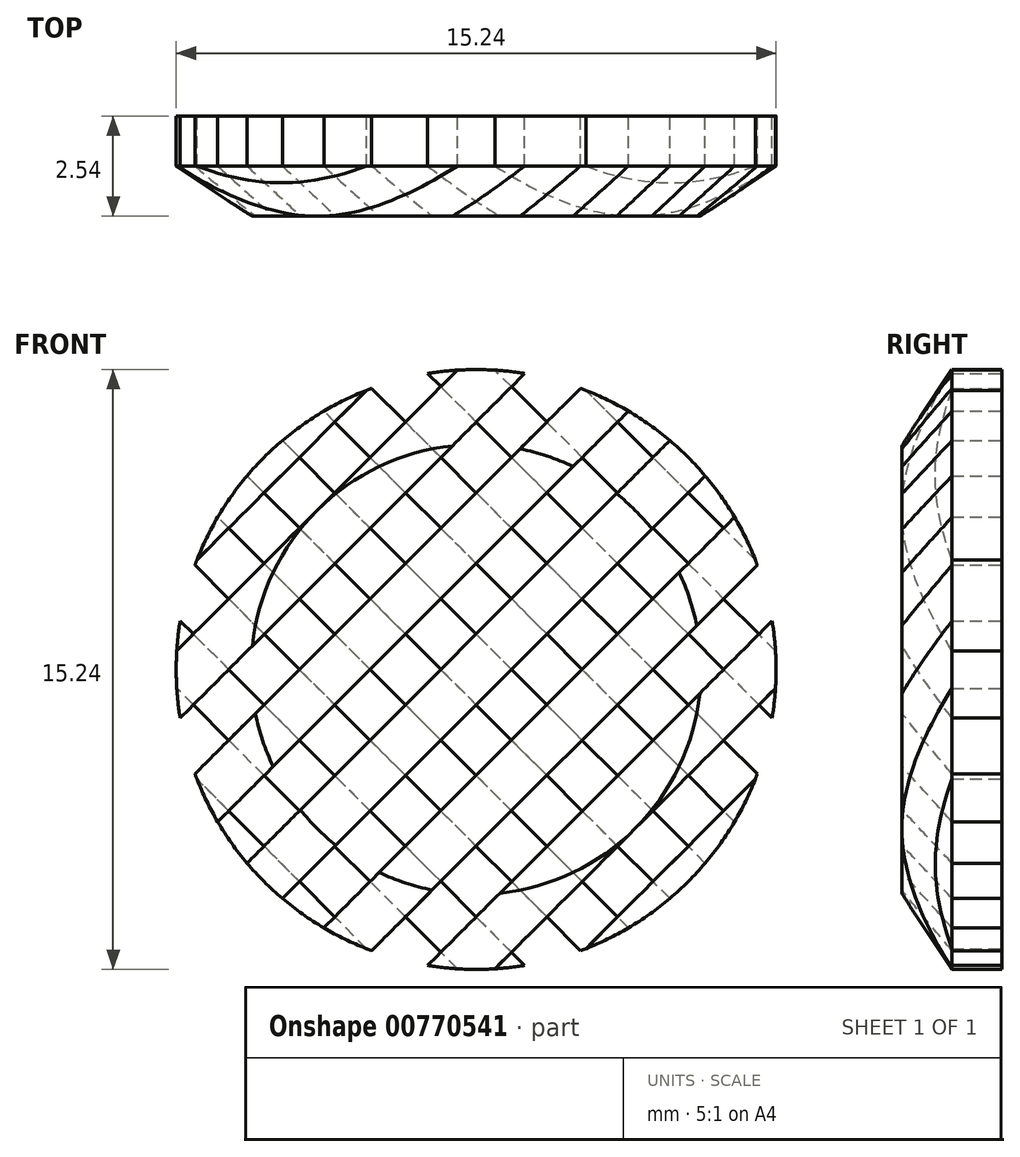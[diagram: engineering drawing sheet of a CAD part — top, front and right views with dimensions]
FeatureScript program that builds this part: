
annotation { "Feature Type Name" : "Feature", "Feature Type Description" : "" }
export const myFeature = defineFeature(function(context is Context, id is Id, definition is map)
    precondition{}
    {
        {
            var Q0;
            Q0=qCreatedBy(makeId("Front.planeOp"),FACE);
            var sketch = newSketch(context, id + "F0", { "sketchPlane" : qUnion([Q0])});
            skCircle(sketch, "E0", {"center": v(0, 0) * mm, "radius": 7.62 * mm});
            skSolve(sketch);
        }
        {
            var Q0;
            Q0=makeQuery(id+"F0.imprint","IMPRINT",FACE,{"disambiguationData":[TD([[makeQuery(id+"F0.imprint","IMPRINT",EDGE,{"derivedFrom":sQuery(id+"F0.wireOp",EDGE,"E0")}),1.0]])]});
            extrude(context, id + "F1", {"entities" : qUnion([Q0]), "endBound" : BoundingType.SYMMETRIC, "depth" : 2.54 * mm, "offsetDistance" : 25.4 * mm});
        }
        {
            var Q0;
            Q0=makeQuery(id+"F1.opExtrude","CAP_FACE",FACE,{"disambiguationData":[OSD([sQuery(id+"F0.wireOp",EDGE,"E0")])],"isStart":false});
            var sketch = newSketch(context, id + "F2", { "sketchPlane" : qUnion([Q0])});
            skArc(sketch, "E1", {"start": v(-7.1, 2.79) * mm, "mid": v(-7.44, 1.65) * mm, "end": v(-7.6, 0.48) * mm});
            skLineSegment(sketch, "E2", {"start": v(-5.39, -5.39) * mm, "end": v(5.39, 5.39) * mm, "construction": true});
            skLineSegment(sketch, "E3", {"start": v(-7.62, 0) * mm, "end": v(7.62, 0) * mm, "construction": true});
            skLineSegment(sketch, "E4", {"start": v(-5.82, -4.92) * mm, "end": v(4.92, 5.82) * mm});
            skLineSegment(sketch, "E5.MirrorCS", {"start": v(-6.29, -4.5) * mm, "end": v(4.5, 6.29) * mm, "construction": true});
            skLineSegment(sketch, "E6.MirrorCS", {"start": v(-6.56, -3.87) * mm, "end": v(3.87, 6.56) * mm});
            skLineSegment(sketch, "E7.MirrorCS", {"start": v(-7.14, -2.65) * mm, "end": v(2.65, 7.14) * mm});
            skLineSegment(sketch, "E8.MirrorCS", {"start": v(-7.52, -1.23) * mm, "end": v(1.23, 7.52) * mm});
            skLineSegment(sketch, "E9.MirrorCS", {"start": v(-7.6, 0.48) * mm, "end": v(-0.48, 7.6) * mm});
            skLineSegment(sketch, "E10.MirrorCS", {"start": v(-7.1, 2.79) * mm, "end": v(-2.79, 7.1) * mm});
            skLineSegment(sketch, "E11.MirrorCS", {"start": v(-4.92, -5.82) * mm, "end": v(5.82, 4.92) * mm});
            skLineSegment(sketch, "E12.MirrorCS", {"start": v(-3.87, -6.56) * mm, "end": v(6.56, 3.87) * mm});
            skLineSegment(sketch, "E13.MirrorCS", {"start": v(-2.65, -7.14) * mm, "end": v(7.14, 2.65) * mm});
            skLineSegment(sketch, "E14.MirrorCS", {"start": v(-1.23, -7.52) * mm, "end": v(7.52, 1.23) * mm});
            skLineSegment(sketch, "E15.MirrorCS", {"start": v(0.48, -7.6) * mm, "end": v(7.6, -0.48) * mm});
            skLineSegment(sketch, "E16.MirrorCS", {"start": v(2.79, -7.1) * mm, "end": v(7.1, -2.79) * mm});
            skArc(sketch, "E17.trimOffspring", {"start": v(-7.52, -1.23) * mm, "mid": v(-7.37, -1.95) * mm, "end": v(-7.14, -2.65) * mm});
            skArc(sketch, "E18.trimOffspring", {"start": v(-6.56, -3.87) * mm, "mid": v(-6.21, -4.41) * mm, "end": v(-5.82, -4.92) * mm});
            skArc(sketch, "E19.trimOffspring", {"start": v(-4.92, -5.82) * mm, "mid": v(-4.41, -6.21) * mm, "end": v(-3.87, -6.56) * mm});
            skArc(sketch, "E20.trimOffspring", {"start": v(-2.65, -7.14) * mm, "mid": v(-1.95, -7.37) * mm, "end": v(-1.23, -7.52) * mm});
            skArc(sketch, "E21.trimOffspring", {"start": v(0.48, -7.6) * mm, "mid": v(1.65, -7.44) * mm, "end": v(2.79, -7.1) * mm});
            skArc(sketch, "E22.trimOffspring", {"start": v(7.1, -2.79) * mm, "mid": v(7.44, -1.65) * mm, "end": v(7.6, -0.48) * mm});
            skArc(sketch, "E23.trimOffspring", {"start": v(7.52, 1.23) * mm, "mid": v(7.37, 1.95) * mm, "end": v(7.14, 2.65) * mm});
            skArc(sketch, "E24.trimOffspring", {"start": v(6.56, 3.87) * mm, "mid": v(6.21, 4.41) * mm, "end": v(5.82, 4.92) * mm});
            skArc(sketch, "E25.trimOffspring", {"start": v(4.92, 5.82) * mm, "mid": v(4.41, 6.21) * mm, "end": v(3.87, 6.56) * mm});
            skArc(sketch, "E26.trimOffspring", {"start": v(2.65, 7.14) * mm, "mid": v(1.95, 7.37) * mm, "end": v(1.23, 7.52) * mm});
            skArc(sketch, "E27.trimOffspring", {"start": v(-0.48, 7.6) * mm, "mid": v(-1.65, 7.44) * mm, "end": v(-2.79, 7.1) * mm});
            skSolve(sketch);
        }
        {
            var Q0;
            Q0=makeQuery(id+"F2.imprint","IMPRINT",FACE,{"disambiguationData":[TD([[makeQuery(id+"F2.imprint","IMPRINT",EDGE,{"derivedFrom":sQuery(id+"F2.wireOp",EDGE,"E15.MirrorCS")}),-1.0]])]});
            var Q1;
            Q1=makeQuery(id+"F2.imprint","IMPRINT",FACE,{"disambiguationData":[TD([[makeQuery(id+"F2.imprint","IMPRINT",EDGE,{"derivedFrom":sQuery(id+"F2.wireOp",EDGE,"E13.MirrorCS")}),-1.0]])]});
            var Q2;
            Q2=makeQuery(id+"F2.imprint","IMPRINT",FACE,{"disambiguationData":[TD([[makeQuery(id+"F2.imprint","IMPRINT",EDGE,{"derivedFrom":sQuery(id+"F2.wireOp",EDGE,"E11.MirrorCS")}),-1.0]])]});
            var Q3;
            Q3=makeQuery(id+"F2.imprint","IMPRINT",FACE,{"disambiguationData":[TD([[makeQuery(id+"F2.imprint","IMPRINT",EDGE,{"derivedFrom":sQuery(id+"F2.wireOp",EDGE,"E4")}),1.0]])]});
            var Q4;
            Q4=makeQuery(id+"F2.imprint","IMPRINT",FACE,{"disambiguationData":[TD([[makeQuery(id+"F2.imprint","IMPRINT",EDGE,{"derivedFrom":sQuery(id+"F2.wireOp",EDGE,"E7.MirrorCS")}),1.0]])]});
            var Q5;
            Q5=makeQuery(id+"F2.imprint","IMPRINT",FACE,{"disambiguationData":[TD([[makeQuery(id+"F2.imprint","IMPRINT",EDGE,{"derivedFrom":sQuery(id+"F2.wireOp",EDGE,"E1")}),1.0]])]});
            extrude(context, id + "F3", {"entities" : qUnion([Q0, Q1, Q2, Q3, Q4, Q5]), "operationType" : NewBodyOperationType.REMOVE, "oppositeDirection" : true, "depth" : 1.27 * mm, "offsetDistance" : 25.4 * mm});
        }
        {
            var Q0;
            Q0=makeQuery(id+"F1.opExtrude","CAP_FACE",FACE,{"disambiguationData":[OSD([sQuery(id+"F0.wireOp",EDGE,"E0")])],"isStart":true});
            var sketch = newSketch(context, id + "F4", { "sketchPlane" : qUnion([Q0])});
            skArc(sketch, "E28", {"start": v(7.1, -2.79) * mm, "mid": v(7.44, -1.65) * mm, "end": v(7.6, -0.48) * mm});
            skLineSegment(sketch, "E29", {"start": v(-5.39, -5.39) * mm, "end": v(5.39, 5.39) * mm, "construction": true});
            skLineSegment(sketch, "E30", {"start": v(-7.62, 0) * mm, "end": v(7.62, 0) * mm, "construction": true});
            skLineSegment(sketch, "E31", {"start": v(-5.82, -4.92) * mm, "end": v(4.92, 5.82) * mm});
            skLineSegment(sketch, "E32.MirrorCS", {"start": v(-6.21, -4.41) * mm, "end": v(4.41, 6.21) * mm, "construction": true});
            skLineSegment(sketch, "E33.MirrorCS", {"start": v(-6.56, -3.87) * mm, "end": v(3.87, 6.56) * mm});
            skLineSegment(sketch, "E34.MirrorCS", {"start": v(-7.14, -2.65) * mm, "end": v(2.65, 7.14) * mm});
            skLineSegment(sketch, "E35.MirrorCS", {"start": v(-7.52, -1.23) * mm, "end": v(1.23, 7.52) * mm});
            skLineSegment(sketch, "E36.MirrorCS", {"start": v(-7.6, 0.48) * mm, "end": v(-0.48, 7.6) * mm});
            skLineSegment(sketch, "E37.MirrorCS", {"start": v(-7.1, 2.79) * mm, "end": v(-2.79, 7.1) * mm});
            skLineSegment(sketch, "E38.MirrorCS", {"start": v(-4.92, -5.82) * mm, "end": v(5.82, 4.92) * mm});
            skLineSegment(sketch, "E39.MirrorCS", {"start": v(-3.87, -6.56) * mm, "end": v(6.56, 3.87) * mm});
            skLineSegment(sketch, "E40.MirrorCS", {"start": v(-2.65, -7.14) * mm, "end": v(7.14, 2.65) * mm});
            skLineSegment(sketch, "E41.MirrorCS", {"start": v(-1.23, -7.52) * mm, "end": v(7.52, 1.23) * mm});
            skLineSegment(sketch, "E42.MirrorCS", {"start": v(0.48, -7.6) * mm, "end": v(7.6, -0.48) * mm});
            skLineSegment(sketch, "E43.MirrorCS", {"start": v(2.79, -7.1) * mm, "end": v(7.1, -2.79) * mm});
            skArc(sketch, "E44.trimOffspring", {"start": v(0.48, -7.6) * mm, "mid": v(1.65, -7.44) * mm, "end": v(2.79, -7.1) * mm});
            skArc(sketch, "E45.trimOffspring", {"start": v(-2.65, -7.14) * mm, "mid": v(-1.95, -7.37) * mm, "end": v(-1.23, -7.52) * mm});
            skArc(sketch, "E46.trimOffspring", {"start": v(7.52, 1.23) * mm, "mid": v(7.37, 1.95) * mm, "end": v(7.14, 2.65) * mm});
            skArc(sketch, "E47.trimOffspring", {"start": v(6.56, 3.87) * mm, "mid": v(6.21, 4.41) * mm, "end": v(5.82, 4.92) * mm});
            skArc(sketch, "E48.trimOffspring", {"start": v(4.92, 5.82) * mm, "mid": v(4.41, 6.21) * mm, "end": v(3.87, 6.56) * mm});
            skArc(sketch, "E49.trimOffspring", {"start": v(2.65, 7.14) * mm, "mid": v(1.95, 7.37) * mm, "end": v(1.23, 7.52) * mm});
            skArc(sketch, "E50.trimOffspring", {"start": v(-0.48, 7.6) * mm, "mid": v(-1.65, 7.44) * mm, "end": v(-2.79, 7.1) * mm});
            skArc(sketch, "E51.trimOffspring", {"start": v(-7.1, 2.79) * mm, "mid": v(-7.44, 1.65) * mm, "end": v(-7.6, 0.48) * mm});
            skArc(sketch, "E52.trimOffspring", {"start": v(-7.52, -1.23) * mm, "mid": v(-7.37, -1.95) * mm, "end": v(-7.14, -2.65) * mm});
            skArc(sketch, "E53.trimOffspring", {"start": v(-6.56, -3.87) * mm, "mid": v(-6.21, -4.41) * mm, "end": v(-5.82, -4.92) * mm});
            skArc(sketch, "E54.trimOffspring", {"start": v(-4.92, -5.82) * mm, "mid": v(-4.41, -6.21) * mm, "end": v(-3.87, -6.56) * mm});
            skSolve(sketch);
        }
        {
            var Q0;
            Q0=makeQuery(id+"F4.imprint","IMPRINT",FACE,{"disambiguationData":[TD([[makeQuery(id+"F4.imprint","IMPRINT",EDGE,{"derivedFrom":sQuery(id+"F4.wireOp",EDGE,"E36.MirrorCS")}),1.0]])]});
            var Q1;
            Q1=makeQuery(id+"F4.imprint","IMPRINT",FACE,{"disambiguationData":[TD([[makeQuery(id+"F4.imprint","IMPRINT",EDGE,{"derivedFrom":sQuery(id+"F4.wireOp",EDGE,"E34.MirrorCS")}),1.0]])]});
            var Q2;
            Q2=makeQuery(id+"F4.imprint","IMPRINT",FACE,{"disambiguationData":[TD([[makeQuery(id+"F4.imprint","IMPRINT",EDGE,{"derivedFrom":sQuery(id+"F4.wireOp",EDGE,"E31")}),1.0]])]});
            var Q3;
            Q3=makeQuery(id+"F4.imprint","IMPRINT",FACE,{"disambiguationData":[TD([[makeQuery(id+"F4.imprint","IMPRINT",EDGE,{"derivedFrom":sQuery(id+"F4.wireOp",EDGE,"E38.MirrorCS")}),-1.0]])]});
            var Q4;
            Q4=makeQuery(id+"F4.imprint","IMPRINT",FACE,{"disambiguationData":[TD([[makeQuery(id+"F4.imprint","IMPRINT",EDGE,{"derivedFrom":sQuery(id+"F4.wireOp",EDGE,"E40.MirrorCS")}),-1.0]])]});
            var Q5;
            Q5=makeQuery(id+"F4.imprint","IMPRINT",FACE,{"disambiguationData":[TD([[makeQuery(id+"F4.imprint","IMPRINT",EDGE,{"derivedFrom":sQuery(id+"F4.wireOp",EDGE,"E28")}),-1.0]])]});
            extrude(context, id + "F5", {"entities" : qUnion([Q0, Q1, Q2, Q3, Q4, Q5]), "operationType" : NewBodyOperationType.REMOVE, "oppositeDirection" : true, "depth" : 1.27 * mm, "offsetDistance" : 25.4 * mm});
        }
        {
            var Q0;
            Q0=qCreatedBy(makeId("Top.planeOp"),FACE);
            var sketch = newSketch(context, id + "F6", { "sketchPlane" : qUnion([Q0])});
            skLineSegment(sketch, "E55", {"start": v(-7.62, 0) * mm, "end": v(-5.71, -1.27) * mm});
            skLineSegment(sketch, "E56", {"start": v(-5.71, -1.27) * mm, "end": v(-7.62, -1.27) * mm});
            skLineSegment(sketch, "E57", {"start": v(-7.62, -1.27) * mm, "end": v(-7.62, 0) * mm});
            skLineSegment(sketch, "E58", {"start": v(0, 0) * mm, "end": v(0, -2.77) * mm, "construction": true});
            skSolve(sketch);
        }
        {
            var Q0;
            Q0 = qSketchRegion(id + "F6", true);
            var Q1;
            Q1=sQuery(id+"F6.wireOp",EDGE,"E58");
            revolve(context, id + "F7", {"operationType" : NewBodyOperationType.REMOVE, "surfaceOperationType" : NewSurfaceOperationType.NEW, "entities" : qUnion([Q0]), "axis" : qUnion([Q1]), "revolveType" : RevolveType.FULL, "oppositeDirection" : true});
        }
    });
